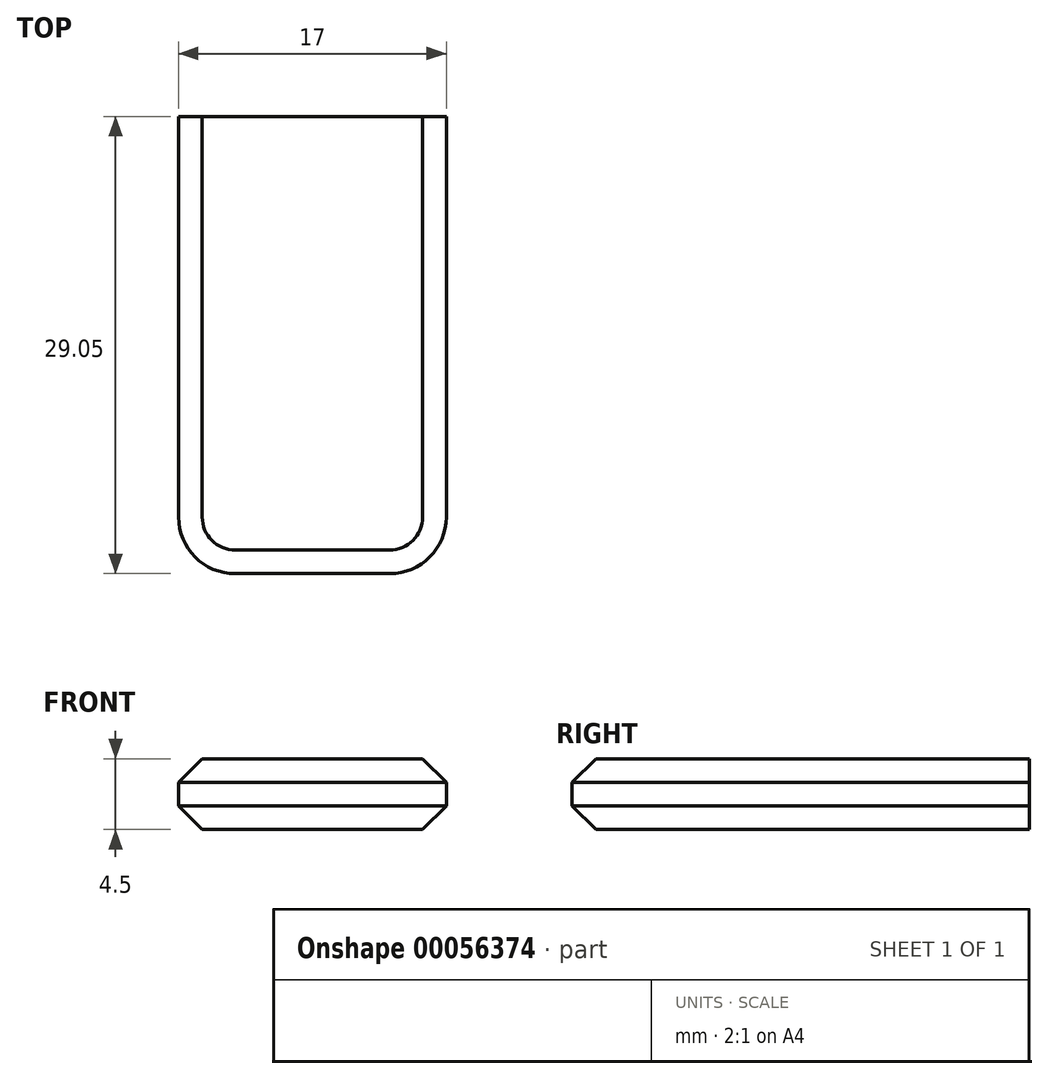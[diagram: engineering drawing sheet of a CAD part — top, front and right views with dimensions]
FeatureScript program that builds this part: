
annotation { "Feature Type Name" : "Feature", "Feature Type Description" : "" }
export const myFeature = defineFeature(function(context is Context, id is Id, definition is map)
    precondition{}
    {
        {
            var Q0;
            Q0=qCreatedBy(makeId("Front.planeOp"),FACE);
            var sketch = newSketch(context, id + "F0", { "sketchPlane" : qUnion([Q0])});
            skLineSegment(sketch, "E0.bottom", {"start": v(-8.5, 2.25) * mm, "end": v(8.5, 2.25) * mm});
            skLineSegment(sketch, "E0.top", {"start": v(-8.5, -2.25) * mm, "end": v(8.5, -2.25) * mm});
            skLineSegment(sketch, "E0.left", {"start": v(-8.5, 2.25) * mm, "end": v(-8.5, -2.25) * mm});
            skLineSegment(sketch, "E0.right", {"start": v(8.5, 2.25) * mm, "end": v(8.5, -2.25) * mm});
            skLineSegment(sketch, "E1", {"start": v(0, 0) * mm, "end": v(23.64, 0) * mm, "construction": true});
            skLineSegment(sketch, "E2", {"start": v(0, 0) * mm, "end": v(0, -12.95) * mm, "construction": true});
            skSolve(sketch);
        }
        {
            var Q0;
            Q0=makeQuery(id+"F0.imprint","IMPRINT",FACE,{"disambiguationData":[TD([[makeQuery(id+"F0.imprint","IMPRINT",EDGE,{"derivedFrom":sQuery(id+"F0.wireOp",EDGE,"E0.bottom")}),-1.0]])]});
            extrude(context, id + "F1", {"entities" : qUnion([Q0]), "depth" : (27.55 + 1.5) * mm, "offsetDistance" : 25 * mm});
        }
        {
            var Q0;
            Q0=makeQuery(id+"F1.opExtrude","CAP_EDGE",EDGE,{"disambiguationData":[OSD([sQuery(id+"F0.wireOp",EDGE,"E0.right")])],"isStart":false});
            var Q1;
            Q1=makeQuery(id+"F1.opExtrude","CAP_EDGE",EDGE,{"disambiguationData":[OSD([sQuery(id+"F0.wireOp",EDGE,"E0.left")])],"isStart":false});
            fillet(context, id + "F2", {"entities" : qUnion([Q0, Q1]), "radius" : (2.1 + 1.5) * mm, "tangentPropagation" : true, "allowEdgeOverflow" : false});
        }
        {
            var Q0;
            Q0=makeQuery(id+"F1.opExtrude","SWEPT_EDGE",EDGE,{"disambiguationData":[OSD([sQuery(id+"F0.wireOp",EDGE,"E0.bottom"),sQuery(id+"F0.wireOp",EDGE,"E0.right")])]});
            var Q1;
            Q1=makeQuery(id+"F1.opExtrude","SWEPT_EDGE",EDGE,{"disambiguationData":[OSD([sQuery(id+"F0.wireOp",EDGE,"E0.top"),sQuery(id+"F0.wireOp",EDGE,"E0.right")])]});
            var Q2;
            Q2=makeQuery(id+"F1.opExtrude","SWEPT_EDGE",EDGE,{"disambiguationData":[OSD([sQuery(id+"F0.wireOp",EDGE,"E0.bottom"),sQuery(id+"F0.wireOp",EDGE,"E0.left")])]});
            var Q3;
            Q3=makeQuery(id+"F1.opExtrude","SWEPT_EDGE",EDGE,{"disambiguationData":[OSD([sQuery(id+"F0.wireOp",EDGE,"E0.top"),sQuery(id+"F0.wireOp",EDGE,"E0.left")])]});
            var Q4;
            Q4=makeQuery(id+"F1.opExtrude","CAP_EDGE",EDGE,{"disambiguationData":[OSD([sQuery(id+"F0.wireOp",EDGE,"E0.bottom")])],"isStart":false});
            var Q5;
            Q5=makeQuery(id+"F1.opExtrude","CAP_FACE",FACE,{"disambiguationData":[OSD([sQuery(id+"F0.wireOp",EDGE,"E0.bottom"),sQuery(id+"F0.wireOp",EDGE,"E0.top"),sQuery(id+"F0.wireOp",EDGE,"E0.left"),sQuery(id+"F0.wireOp",EDGE,"E0.right")])],"isStart":false});
            chamfer(context, id + "F3", {"entities" : qUnion([Q0, Q1, Q2, Q3, Q4, Q5]), "width" : 1.5 * mm, "tangentPropagation" : true});
        }
    });
